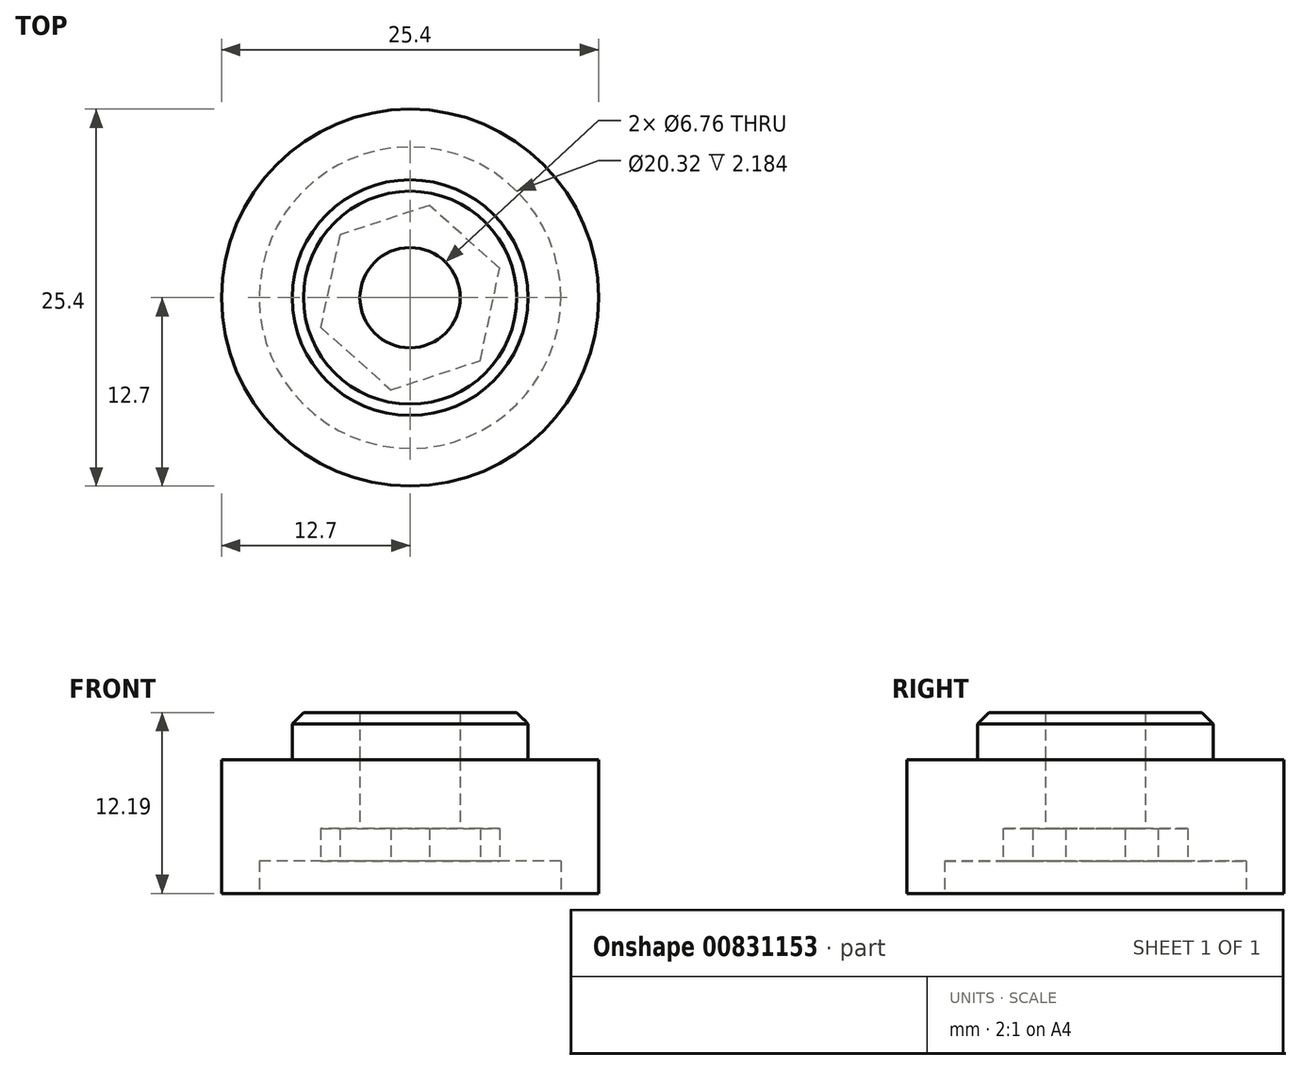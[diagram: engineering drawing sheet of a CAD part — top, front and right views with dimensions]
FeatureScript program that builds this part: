
annotation { "Feature Type Name" : "Feature", "Feature Type Description" : "" }
export const myFeature = defineFeature(function(context is Context, id is Id, definition is map)
    precondition{}
    {
        {
            var Q0;
            Q0=qCreatedBy(makeId("Top.planeOp"),FACE);
            var sketch = newSketch(context, id + "F0", { "sketchPlane" : qUnion([Q0])});
            skCircle(sketch, "E0", {"center": v(0, 0) * mm, "radius": 12.7 * mm});
            skSolve(sketch);
        }
        {
            var Q0;
            Q0=makeQuery(id+"F0.imprint","IMPRINT",FACE,{"disambiguationData":[TD([[makeQuery(id+"F0.imprint","IMPRINT",EDGE,{"derivedFrom":sQuery(id+"F0.wireOp",EDGE,"E0")}),1.0]])]});
            extrude(context, id + "F1", {"entities" : qUnion([Q0]), "depth" : 9.02 * mm, "offsetDistance" : 25.4 * mm});
        }
        {
            var Q0;
            Q0=makeQuery(id+"F1.opExtrude","CAP_FACE",FACE,{"disambiguationData":[OSD([sQuery(id+"F0.wireOp",EDGE,"E0")])],"isStart":false});
            var sketch = newSketch(context, id + "F2", { "sketchPlane" : qUnion([Q0])});
            skCircle(sketch, "E1", {"center": v(0, 0) * mm, "radius": 7.94 * mm});
            skSolve(sketch);
        }
        {
            var Q0;
            Q0=makeQuery(id+"F2.imprint","IMPRINT",FACE,{"disambiguationData":[TD([[makeQuery(id+"F2.imprint","IMPRINT",EDGE,{"derivedFrom":sQuery(id+"F2.wireOp",EDGE,"E1")}),1.0]])]});
            extrude(context, id + "F3", {"entities" : qUnion([Q0]), "depth" : 3.17 * mm, "offsetDistance" : 25.4 * mm});
        }
        {
            var Q0;
            Q0=makeQuery(id+"F3.opExtrude","CAP_EDGE",EDGE,{"disambiguationData":[OSD([sQuery(id+"F2.wireOp",EDGE,"E1")])],"isStart":false});
            chamfer(context, id + "F4", {"entities" : qUnion([Q0]), "width" : 0.76 * mm, "tangentPropagation" : true});
        }
        {
            var Q0;
            Q0=makeQuery(id+"F0.imprint","IMPRINT",FACE,{"disambiguationData":[TD([[makeQuery(id+"F0.imprint","IMPRINT",EDGE,{"derivedFrom":sQuery(id+"F0.wireOp",EDGE,"E0")}),1.0]])]});
            var sketch = newSketch(context, id + "F5", { "sketchPlane" : qUnion([Q0])});
            skCircle(sketch, "E2", {"center": v(0, 0) * mm, "radius": 10.16 * mm});
            skSolve(sketch);
        }
        {
            var Q0;
            Q0 = qSketchRegion(id + "F5", true);
            extrude(context, id + "F6", {"entities" : qUnion([Q0]), "operationType" : NewBodyOperationType.REMOVE, "depth" : 2.18 * mm, "offsetDistance" : 25.4 * mm});
        }
        {
            var Q0;
            Q0=makeQuery(id+"F0.imprint","IMPRINT",FACE,{"disambiguationData":[TD([[makeQuery(id+"F0.imprint","IMPRINT",EDGE,{"derivedFrom":sQuery(id+"F0.wireOp",EDGE,"E0")}),1.0]])]});
            var sketch = newSketch(context, id + "F7", { "sketchPlane" : qUnion([Q0])});
            skCircle(sketch, "E3.cCircle", {"center": v(0, 0) * mm, "radius": 5.5 * mm, "construction": true});
            skLineSegment(sketch, "E3.0", {"start": v(1.3, 6.22) * mm, "end": v(6.03, 1.99) * mm});
            skLineSegment(sketch, "E3.1", {"start": v(6.03, 1.99) * mm, "end": v(4.74, -4.23) * mm});
            skLineSegment(sketch, "E3.2", {"start": v(4.74, -4.23) * mm, "end": v(-1.3, -6.22) * mm});
            skLineSegment(sketch, "E3.3", {"start": v(-1.3, -6.22) * mm, "end": v(-6.03, -1.99) * mm});
            skLineSegment(sketch, "E3.4", {"start": v(-6.03, -1.99) * mm, "end": v(-4.74, 4.23) * mm});
            skLineSegment(sketch, "E3.5", {"start": v(-4.74, 4.23) * mm, "end": v(1.3, 6.22) * mm});
            skPoint(sketch, "E3.0.midPoint", {"position": v(3.66, 4.1) * mm});
            skSolve(sketch);
        }
        {
            var Q0;
            Q0 = qSketchRegion(id + "F7", true);
            extrude(context, id + "F8", {"entities" : qUnion([Q0]), "operationType" : NewBodyOperationType.REMOVE, "depth" : 4.37 * mm, "offsetDistance" : 25.4 * mm});
        }
        {
            var Q0;
            Q0=sQuery(id+"F0.wireOp",VERTEX,"E0.center");
            var Q1;
            Q1=makeQuery(id+"F3.opExtrude","SWEPT_BODY",BODY,{"disambiguationData":[OSD([sQuery(id+"F2.wireOp",EDGE,"E1")])]});
            var Q2;
            Q2=makeQuery(id+"F1.opExtrude","SWEPT_BODY",BODY,{"disambiguationData":[OSD([sQuery(id+"F0.wireOp",EDGE,"E0")])]});
            hole(context, id + "F9", {"style" : HoleStyle.SIMPLE, "endStyle" : HoleEndStyle.THROUGH, "oppositeDirection" : true, "holeDiameter" : 6.76 * mm, "majorDiameter" : 6.35 * mm, "isTappedThrough" : true, "tappedDepth" : 12.7 * mm, "tapClearance" : 3, "locations" : qUnion([Q0]), "scope" : qUnion([Q1, Q2])});
        }
    });
